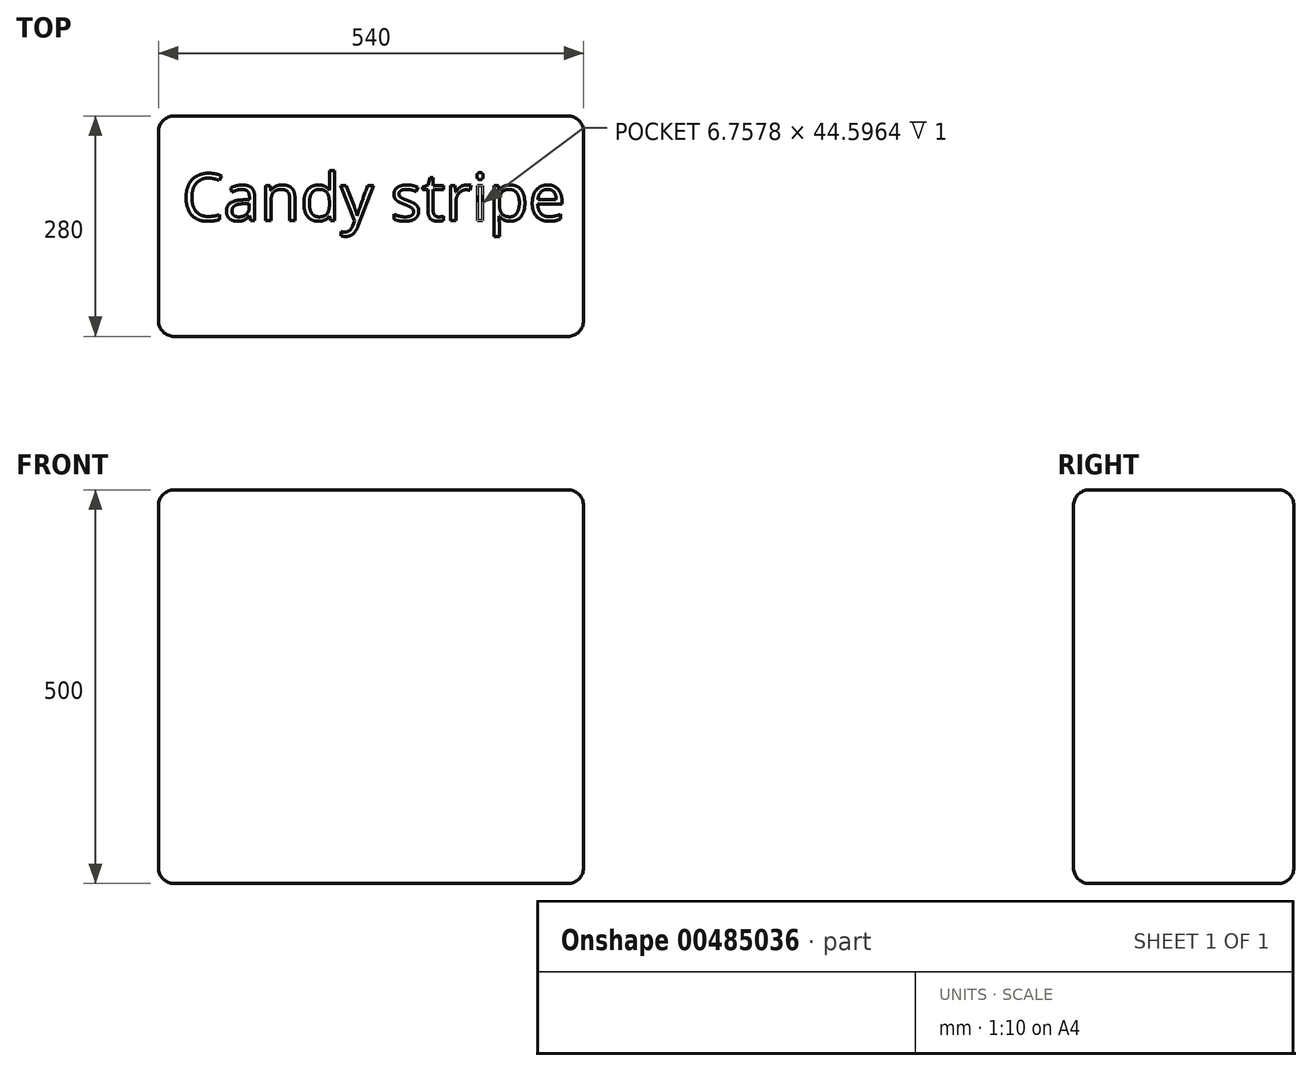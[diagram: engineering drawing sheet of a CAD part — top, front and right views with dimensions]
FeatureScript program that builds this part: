
annotation { "Feature Type Name" : "Feature", "Feature Type Description" : "" }
export const myFeature = defineFeature(function(context is Context, id is Id, definition is map)
    precondition{}
    {
        {
            var Q0;
            Q0=qCreatedBy(makeId("Top.planeOp"),FACE);
            var sketch = newSketch(context, id + "F0", { "sketchPlane" : qUnion([Q0])});
            skLineSegment(sketch, "E0.bottom", {"start": v(270, -140) * mm, "end": v(-270, -140) * mm});
            skLineSegment(sketch, "E0.top", {"start": v(270, 140) * mm, "end": v(-270, 140) * mm});
            skLineSegment(sketch, "E0.left", {"start": v(270, -140) * mm, "end": v(270, 140) * mm});
            skLineSegment(sketch, "E0.right", {"start": v(-270, -140) * mm, "end": v(-270, 140) * mm});
            skPoint(sketch, "E0.middle", {"position": v(0, 0) * mm});
            skSolve(sketch);
        }
        {
            var Q0;
            Q0 = qSketchRegion(id + "F0", true);
            extrude(context, id + "F1", {"entities" : qUnion([Q0]), "depth" : 500 * mm, "offsetDistance" : 25 * mm});
        }
        {
            var Q0;
            Q0=makeQuery(id+"F1.opExtrude","CAP_FACE",FACE,{"disambiguationData":[OSD([sQuery(id+"F0.wireOp",EDGE,"E0.bottom"),sQuery(id+"F0.wireOp",EDGE,"E0.top"),sQuery(id+"F0.wireOp",EDGE,"E0.left"),sQuery(id+"F0.wireOp",EDGE,"E0.right")])],"isStart":false});
            var Q1;
            Q1=makeQuery(id+"F1.opExtrude","SWEPT_EDGE",EDGE,{"disambiguationData":[OSD([sQuery(id+"F0.wireOp",EDGE,"E0.top"),sQuery(id+"F0.wireOp",EDGE,"E0.left")])]});
            var Q2;
            Q2=makeQuery(id+"F1.opExtrude","CAP_FACE",FACE,{"disambiguationData":[OSD([sQuery(id+"F0.wireOp",EDGE,"E0.bottom"),sQuery(id+"F0.wireOp",EDGE,"E0.top"),sQuery(id+"F0.wireOp",EDGE,"E0.left"),sQuery(id+"F0.wireOp",EDGE,"E0.right")])],"isStart":true});
            var Q3;
            Q3=makeQuery(id+"F1.opExtrude","SWEPT_EDGE",EDGE,{"disambiguationData":[OSD([sQuery(id+"F0.wireOp",EDGE,"E0.bottom"),sQuery(id+"F0.wireOp",EDGE,"E0.right")])]});
            var Q4;
            Q4=makeQuery(id+"F1.opExtrude","SWEPT_FACE",FACE,{"disambiguationData":[OSD([sQuery(id+"F0.wireOp",EDGE,"E0.bottom")])]});
            var Q5;
            Q5=makeQuery(id+"F1.opExtrude","SWEPT_EDGE",EDGE,{"disambiguationData":[OSD([sQuery(id+"F0.wireOp",EDGE,"E0.bottom"),sQuery(id+"F0.wireOp",EDGE,"E0.left")])]});
            var Q6;
            Q6=makeQuery(id+"F1.opExtrude","CAP_EDGE",EDGE,{"disambiguationData":[OSD([sQuery(id+"F0.wireOp",EDGE,"E0.bottom")])],"isStart":true});
            var Q7;
            Q7=makeQuery(id+"F1.opExtrude","SWEPT_FACE",FACE,{"disambiguationData":[OSD([sQuery(id+"F0.wireOp",EDGE,"E0.left")])]});
            var Q8;
            Q8=makeQuery(id+"F1.opExtrude","CAP_EDGE",EDGE,{"disambiguationData":[OSD([sQuery(id+"F0.wireOp",EDGE,"E0.bottom")])],"isStart":false});
            var Q9;
            Q9=makeQuery(id+"F1.opExtrude","CAP_EDGE",EDGE,{"disambiguationData":[OSD([sQuery(id+"F0.wireOp",EDGE,"E0.top")])],"isStart":false});
            var Q10;
            Q10=makeQuery(id+"F1.opExtrude","CAP_EDGE",EDGE,{"disambiguationData":[OSD([sQuery(id+"F0.wireOp",EDGE,"E0.left")])],"isStart":true});
            var Q11;
            Q11=makeQuery(id+"F1.opExtrude","CAP_EDGE",EDGE,{"disambiguationData":[OSD([sQuery(id+"F0.wireOp",EDGE,"E0.left")])],"isStart":false});
            var Q12;
            Q12=makeQuery(id+"F1.opExtrude","CAP_EDGE",EDGE,{"disambiguationData":[OSD([sQuery(id+"F0.wireOp",EDGE,"E0.right")])],"isStart":false});
            var Q13;
            Q13=makeQuery(id+"F1.opExtrude","SWEPT_EDGE",EDGE,{"disambiguationData":[OSD([sQuery(id+"F0.wireOp",EDGE,"E0.top"),sQuery(id+"F0.wireOp",EDGE,"E0.right")])]});
            var Q14;
            Q14=makeQuery(id+"F1.opExtrude","SWEPT_FACE",FACE,{"disambiguationData":[OSD([sQuery(id+"F0.wireOp",EDGE,"E0.right")])]});
            var Q15;
            Q15=makeQuery(id+"F1.opExtrude","CAP_EDGE",EDGE,{"disambiguationData":[OSD([sQuery(id+"F0.wireOp",EDGE,"E0.top")])],"isStart":true});
            var Q16;
            Q16=makeQuery(id+"F1.opExtrude","CAP_EDGE",EDGE,{"disambiguationData":[OSD([sQuery(id+"F0.wireOp",EDGE,"E0.right")])],"isStart":true});
            var Q17;
            Q17=makeQuery(id+"F1.opExtrude","SWEPT_FACE",FACE,{"disambiguationData":[OSD([sQuery(id+"F0.wireOp",EDGE,"E0.top")])]});
            fillet(context, id + "F2", {"entities" : qUnion([Q0, Q1, Q2, Q3, Q4, Q5, Q6, Q7, Q8, Q9, Q10, Q11, Q12, Q13, Q14, Q15, Q16, Q17]), "radius" : 20 * mm, "tangentPropagation" : true, "allowEdgeOverflow" : false});
        }
        {
            var Q0;
            Q0=makeQuery(id+"F1.opExtrude","CAP_FACE",FACE,{"disambiguationData":[OSD([sQuery(id+"F0.wireOp",EDGE,"E0.bottom"),sQuery(id+"F0.wireOp",EDGE,"E0.top"),sQuery(id+"F0.wireOp",EDGE,"E0.left"),sQuery(id+"F0.wireOp",EDGE,"E0.right")])],"isStart":false});
            var sketch = newSketch(context, id + "F3", { "sketchPlane" : qUnion([Q0])});
            skText(sketch, "E1", { "text": "Candy stripe", "fontName": "OpenSans-Regular.ttf"});
            const initialGuessF3  = {"E1": [-0.24, 0.00704, 1, 0, 0.06]};
            skSetInitialGuess(sketch, initialGuessF3);
            skSolve(sketch);
        }
        {
            var Q0;
            Q0 = qSketchRegion(id + "F3", true);
            extrude(context, id + "F4", {"entities" : qUnion([Q0]), "operationType" : NewBodyOperationType.REMOVE, "oppositeDirection" : true, "depth" : 1 * mm});
        }
    });
